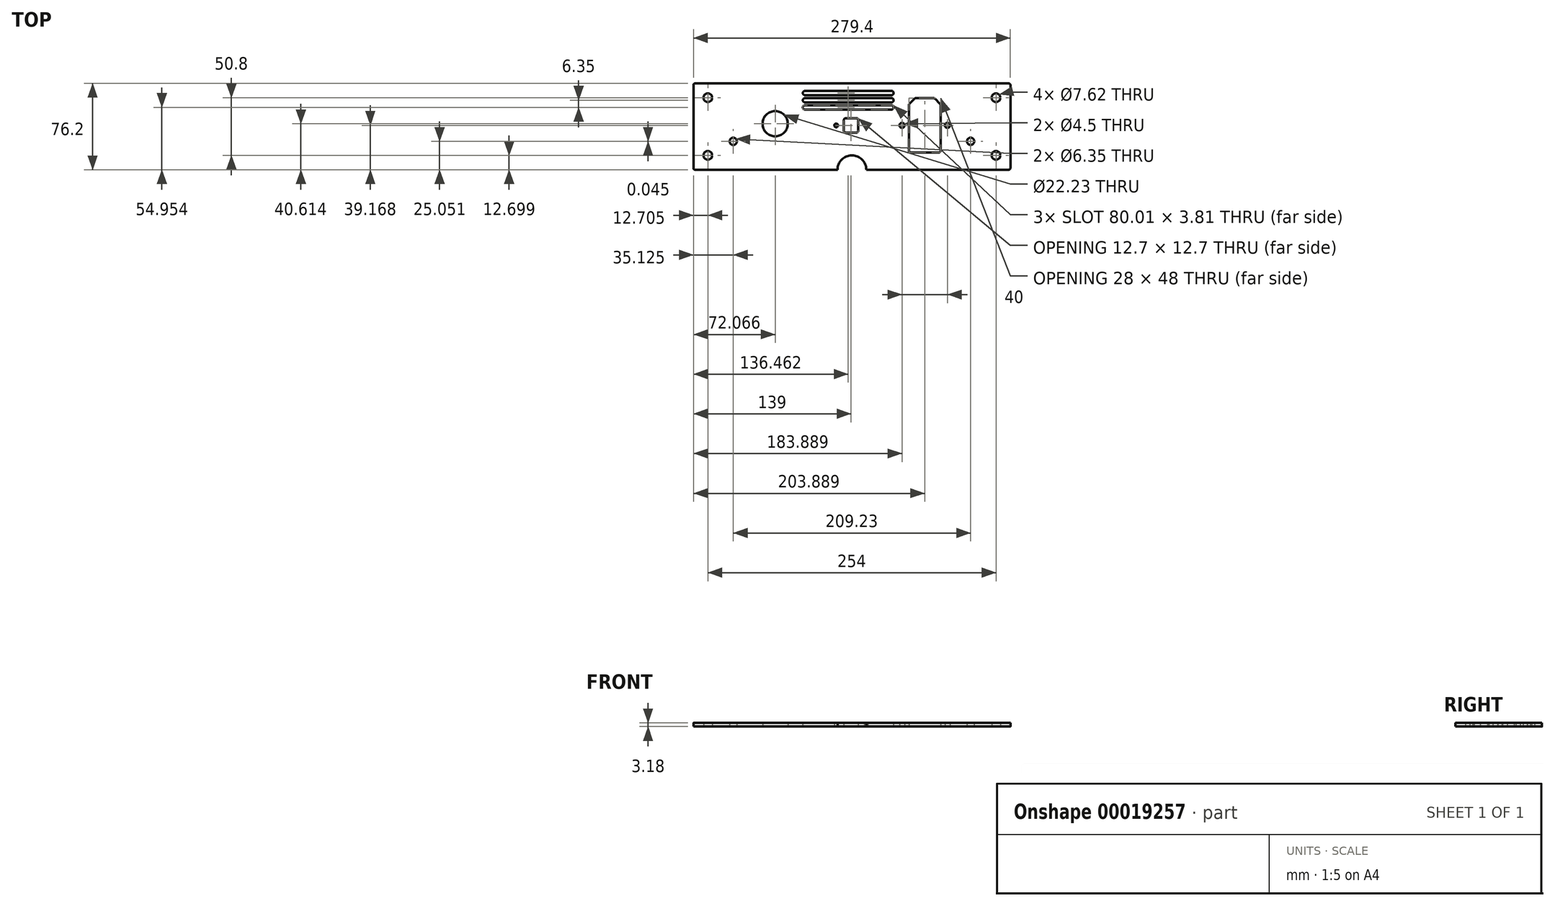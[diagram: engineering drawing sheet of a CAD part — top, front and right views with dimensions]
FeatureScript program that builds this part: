
annotation { "Feature Type Name" : "Feature", "Feature Type Description" : "" }
export const myFeature = defineFeature(function(context is Context, id is Id, definition is map)
    precondition{}
    {
        {
            var Q0;
            Q0=qCreatedBy(makeId("Top.planeOp"),FACE);
            var sketch = newSketch(context, id + "F0", { "sketchPlane" : qUnion([Q0])});
            skLineSegment(sketch, "E0.bottom", {"start": v(-124.13, 36.53) * mm, "end": v(152.02, 36.53) * mm});
            skLineSegment(sketch, "E0.left", {"start": v(-125.76, 34.9) * mm, "end": v(-125.76, -38.05) * mm});
            skLineSegment(sketch, "E0.right", {"start": v(153.64, 34.9) * mm, "end": v(153.64, -38.05) * mm});
            skLineSegment(sketch, "E1", {"start": v(-100.36, 36.53) * mm, "end": v(-100.36, -39.67) * mm, "construction": true});
            skLineSegment(sketch, "E2", {"start": v(128.24, 36.53) * mm, "end": v(128.24, -39.67) * mm, "construction": true});
            skCircle(sketch, "E3", {"center": v(-113.06, 23.83) * mm, "radius": 3.81 * mm});
            skCircle(sketch, "E4", {"center": v(-113.06, -26.97) * mm, "radius": 3.81 * mm});
            skCircle(sketch, "E5", {"center": v(140.94, 23.83) * mm, "radius": 3.81 * mm});
            skCircle(sketch, "E6", {"center": v(140.94, -26.97) * mm, "radius": 3.81 * mm});
            skLineSegment(sketch, "E7", {"start": v(-125.76, -24.75) * mm, "end": v(153.64, -24.75) * mm, "construction": true});
            skCircle(sketch, "E8", {"center": v(-53.7, 0.94) * mm, "radius": 11.11 * mm});
            skLineSegment(sketch, "E9.bottom", {"start": v(110.02, -4.48) * mm, "end": v(127.17, -4.48) * mm, "construction": true});
            skLineSegment(sketch, "E9.top", {"start": v(110.02, -24.67) * mm, "end": v(127.17, -24.67) * mm, "construction": true});
            skLineSegment(sketch, "E9.left", {"start": v(110.02, -4.48) * mm, "end": v(110.02, -24.67) * mm, "construction": true});
            skLineSegment(sketch, "E9.right", {"start": v(127.17, -4.48) * mm, "end": v(127.17, -24.67) * mm, "construction": true});
            skLineSegment(sketch, "E10.bottom", {"start": v(-99.2, -4.52) * mm, "end": v(-82.06, -4.52) * mm, "construction": true});
            skLineSegment(sketch, "E10.top", {"start": v(-99.2, -24.72) * mm, "end": v(-82.06, -24.72) * mm, "construction": true});
            skLineSegment(sketch, "E10.right", {"start": v(-82.06, -4.52) * mm, "end": v(-82.06, -24.72) * mm, "construction": true});
            skLineSegment(sketch, "E10.left", {"start": v(-99.2, -4.52) * mm, "end": v(-99.2, -24.72) * mm, "construction": true});
            skPoint(sketch, "E11.visualSharp", {"position": v(-125.76, 36.53) * mm});
            skArc(sketch, "E11.filletArc", {"start": v(-124.13, 36.53) * mm, "mid": v(-125.28, 36.05) * mm, "end": v(-125.76, 34.9) * mm});
            skPoint(sketch, "E12.visualSharp", {"position": v(-125.76, -39.67) * mm});
            skArc(sketch, "E12.filletArc", {"start": v(-125.76, -38.05) * mm, "mid": v(-125.28, -39.2) * mm, "end": v(-124.13, -39.67) * mm});
            skPoint(sketch, "E13.visualSharp", {"position": v(153.64, 36.53) * mm});
            skArc(sketch, "E13.filletArc", {"start": v(153.64, 34.9) * mm, "mid": v(153.17, 36.05) * mm, "end": v(152.02, 36.53) * mm});
            skPoint(sketch, "E14.visualSharp", {"position": v(153.64, -39.67) * mm});
            skArc(sketch, "E14.filletArc", {"start": v(152.02, -39.67) * mm, "mid": v(153.17, -39.2) * mm, "end": v(153.64, -38.05) * mm});
            skCircle(sketch, "E15", {"center": v(26.4, -0.6) * mm, "radius": 1.65 * mm});
            skCircle(sketch, "E16", {"center": v(0.08, -0.6) * mm, "radius": 1.65 * mm});
            skCircle(sketch, "E17", {"center": v(-53.7, 0.94) * mm, "radius": 19.98 * mm, "construction": true});
            skCircle(sketch, "E18", {"center": v(-90.64, -14.62) * mm, "radius": 3.18 * mm});
            skCircle(sketch, "E19", {"center": v(118.6, -14.57) * mm, "radius": 3.18 * mm});
            skLineSegment(sketch, "E20.bottom", {"start": v(70.46, 23.5) * mm, "end": v(85.8, 23.5) * mm});
            skLineSegment(sketch, "E20.top", {"start": v(65.75, -24.5) * mm, "end": v(90.5, -24.5) * mm});
            skLineSegment(sketch, "E20.left", {"start": v(64.13, 17.17) * mm, "end": v(64.13, -22.88) * mm});
            skLineSegment(sketch, "E20.right", {"start": v(92.13, 17.17) * mm, "end": v(92.13, -22.88) * mm});
            skLineSegment(sketch, "E21", {"start": v(78.13, -0.5) * mm, "end": v(98.13, -0.5) * mm, "construction": true});
            skLineSegment(sketch, "E22", {"start": v(78.13, -0.5) * mm, "end": v(58.13, -0.5) * mm, "construction": true});
            skCircle(sketch, "E23", {"center": v(58.13, -0.5) * mm, "radius": 2.25 * mm});
            skCircle(sketch, "E24", {"center": v(98.13, -0.5) * mm, "radius": 2.25 * mm});
            skLineSegment(sketch, "E25.bottom", {"start": v(8.52, 5.76) * mm, "end": v(17.96, 5.76) * mm});
            skLineSegment(sketch, "E25.top", {"start": v(8.52, -6.94) * mm, "end": v(17.96, -6.94) * mm});
            skLineSegment(sketch, "E25.left", {"start": v(6.9, 4.13) * mm, "end": v(6.9, -5.32) * mm});
            skLineSegment(sketch, "E25.right", {"start": v(19.6, 4.13) * mm, "end": v(19.6, -5.32) * mm});
            skLineSegment(sketch, "E26", {"start": v(-125.76, 11.13) * mm, "end": v(-100.36, 11.13) * mm, "construction": true});
            skLineSegment(sketch, "E27", {"start": v(-100.36, 11.13) * mm, "end": v(-125.76, 36.53) * mm, "construction": true});
            skLineSegment(sketch, "E28", {"start": v(-125.76, -14.27) * mm, "end": v(-100.36, -14.27) * mm, "construction": true});
            skLineSegment(sketch, "E29", {"start": v(-125.76, -14.27) * mm, "end": v(-100.36, -39.67) * mm, "construction": true});
            skLineSegment(sketch, "E30", {"start": v(-124.13, -39.67) * mm, "end": v(1.24, -39.67) * mm});
            skArc(sketch, "E31", {"start": v(26.64, -39.67) * mm, "mid": v(13.94, -26.97) * mm, "end": v(1.24, -39.67) * mm});
            skLineSegment(sketch, "E32.trimOffspring", {"start": v(26.64, -39.67) * mm, "end": v(152.02, -39.67) * mm});
            skLineSegment(sketch, "E33", {"start": v(64.6, 18.32) * mm, "end": v(69.31, 23.02) * mm});
            skLineSegment(sketch, "E34", {"start": v(86.95, 23.02) * mm, "end": v(91.65, 18.32) * mm});
            skLineSegment(sketch, "E35", {"start": v(0.08, -0.6) * mm, "end": v(26.4, -0.6) * mm, "construction": true});
            skLineSegment(sketch, "E36", {"start": v(13.24, 5.76) * mm, "end": v(13.24, -6.94) * mm, "construction": true});
            skLineSegment(sketch, "E37.0.right", {"start": v(-27.4, 26.08) * mm, "end": v(48.8, 26.08) * mm});
            skLineSegment(sketch, "E37.0.left", {"start": v(-27.4, 29.89) * mm, "end": v(48.8, 29.89) * mm});
            skLineSegment(sketch, "E38.direction1", {"start": v(-27.4, 15.28) * mm, "end": v(-27.4, 15.28) * mm});
            skLineSegment(sketch, "E38.0.2.0", {"start": v(-27.4, 27.98) * mm, "end": v(48.8, 27.98) * mm, "construction": true});
            skLineSegment(sketch, "E38.0.1.0", {"start": v(-27.4, 21.63) * mm, "end": v(48.8, 21.63) * mm, "construction": true});
            skLineSegment(sketch, "E37.1.left", {"start": v(-27.4, 23.54) * mm, "end": v(48.8, 23.54) * mm});
            skLineSegment(sketch, "E39.0.right", {"start": v(-27.4, 13.38) * mm, "end": v(48.8, 13.38) * mm});
            skLineSegment(sketch, "E39.0.left", {"start": v(-27.4, 17.19) * mm, "end": v(48.8, 17.19) * mm});
            skLineSegment(sketch, "E40", {"start": v(-27.4, 15.28) * mm, "end": v(48.8, 15.28) * mm, "construction": true});
            skLineSegment(sketch, "E37.1.right", {"start": v(-27.4, 19.73) * mm, "end": v(48.8, 19.73) * mm});
            skArc(sketch, "E39.0.endCap", {"start": v(48.8, 17.19) * mm, "mid": v(50.7, 15.28) * mm, "end": v(48.8, 13.38) * mm});
            skArc(sketch, "E37.1.endCap", {"start": v(48.8, 23.54) * mm, "mid": v(50.7, 21.63) * mm, "end": v(48.8, 19.73) * mm});
            skArc(sketch, "E37.0.endCap", {"start": v(48.8, 29.89) * mm, "mid": v(50.7, 27.98) * mm, "end": v(48.8, 26.08) * mm});
            skArc(sketch, "E37.1.startCap", {"start": v(-27.4, 19.73) * mm, "mid": v(-29.3, 21.63) * mm, "end": v(-27.4, 23.54) * mm});
            skArc(sketch, "E37.0.startCap", {"start": v(-27.4, 26.08) * mm, "mid": v(-29.3, 27.98) * mm, "end": v(-27.4, 29.89) * mm});
            skArc(sketch, "E39.0.startCap", {"start": v(-27.4, 13.38) * mm, "mid": v(-29.3, 15.28) * mm, "end": v(-27.4, 17.19) * mm});
            skPoint(sketch, "E41.visualSharp", {"position": v(6.9, 5.76) * mm});
            skArc(sketch, "E41.filletArc", {"start": v(8.52, 5.76) * mm, "mid": v(7.37, 5.28) * mm, "end": v(6.9, 4.13) * mm});
            skPoint(sketch, "E42.visualSharp", {"position": v(19.6, 5.76) * mm});
            skArc(sketch, "E42.filletArc", {"start": v(19.6, 4.13) * mm, "mid": v(19.11, 5.28) * mm, "end": v(17.96, 5.76) * mm});
            skPoint(sketch, "E43.visualSharp", {"position": v(19.6, -6.94) * mm});
            skArc(sketch, "E43.filletArc", {"start": v(17.96, -6.94) * mm, "mid": v(19.11, -6.47) * mm, "end": v(19.6, -5.32) * mm});
            skPoint(sketch, "E44.visualSharp", {"position": v(6.9, -6.94) * mm});
            skArc(sketch, "E44.filletArc", {"start": v(6.9, -5.32) * mm, "mid": v(7.37, -6.47) * mm, "end": v(8.52, -6.94) * mm});
            skPoint(sketch, "E45.visualSharp", {"position": v(64.13, 17.84) * mm});
            skArc(sketch, "E45.filletArc", {"start": v(64.6, 18.32) * mm, "mid": v(64.25, 17.8) * mm, "end": v(64.13, 17.17) * mm});
            skPoint(sketch, "E46.visualSharp", {"position": v(69.79, 23.5) * mm});
            skArc(sketch, "E46.filletArc", {"start": v(70.46, 23.5) * mm, "mid": v(69.84, 23.37) * mm, "end": v(69.31, 23.02) * mm});
            skPoint(sketch, "E47.visualSharp", {"position": v(86.47, 23.5) * mm});
            skArc(sketch, "E47.filletArc", {"start": v(86.95, 23.02) * mm, "mid": v(86.42, 23.37) * mm, "end": v(85.8, 23.5) * mm});
            skPoint(sketch, "E48.visualSharp", {"position": v(92.13, 17.84) * mm});
            skArc(sketch, "E48.filletArc", {"start": v(92.13, 17.17) * mm, "mid": v(92, 17.8) * mm, "end": v(91.65, 18.32) * mm});
            skPoint(sketch, "E49.visualSharp", {"position": v(92.13, -24.5) * mm});
            skArc(sketch, "E49.filletArc", {"start": v(90.5, -24.5) * mm, "mid": v(91.65, -24.03) * mm, "end": v(92.13, -22.88) * mm});
            skPoint(sketch, "E50.visualSharp", {"position": v(64.13, -24.5) * mm});
            skArc(sketch, "E50.filletArc", {"start": v(64.13, -22.88) * mm, "mid": v(64.6, -24.03) * mm, "end": v(65.75, -24.5) * mm});
            skSolve(sketch);
        }
        {
            var Q0;
            Q0=qSketchRegion(id+"F0",true);
            var Q1;
            {var subQ0=sQuery(id+"F0.wireOp",EDGE,"2bf4d64c-811b-49e9-8bac-2fb631b87969");Q1=makeQuery(id+"F0.imprint","IMPRINT",FACE,{"disambiguationData":[TD([[makeQuery(id+"F0.imprint","IMPRINT",EDGE,{"derivedFrom":subQ0}),-1.0]])]});}
            var Q2;
            Q2=makeQuery(id+"F0.imprint","IMPRINT",FACE,{"disambiguationData":[TD([[makeQuery(id+"F0.imprint","IMPRINT",EDGE,{"derivedFrom":sQuery(id+"F0.wireOp",EDGE,"E4")}),-1.0]])]});
            var Q3;
            Q3=makeQuery(id+"F0.imprint","IMPRINT",FACE,{"disambiguationData":[TD([[makeQuery(id+"F0.imprint","IMPRINT",EDGE,{"derivedFrom":sQuery(id+"F0.wireOp",EDGE,"2008dfa9-6c35-4ba0-b188-531ab9956baa.sketch_text.stroke-44")}),-1.0]])]});
            var Q4;
            Q4=makeQuery(id+"F0.imprint","IMPRINT",FACE,{"disambiguationData":[TD([[makeQuery(id+"F0.imprint","IMPRINT",EDGE,{"derivedFrom":sQuery(id+"F0.wireOp",EDGE,"eab93db6-d5a0-4661-8d19-a60daf389fbf.sketch_text.stroke-16")}),1.0]])]});
            var Q5;
            Q5=makeQuery(id+"F0.imprint","IMPRINT",FACE,{"disambiguationData":[TD([[makeQuery(id+"F0.imprint","IMPRINT",EDGE,{"derivedFrom":sQuery(id+"F0.wireOp",EDGE,"E9.bottom")}),1.0]])]});
            var Q6;
            Q6=makeQuery(id+"F0.imprint","IMPRINT",FACE,{"disambiguationData":[TD([[makeQuery(id+"F0.imprint","IMPRINT",EDGE,{"derivedFrom":sQuery(id+"F0.wireOp",EDGE,"6bf0a539-61ef-4557-94e5-60696c5db384.bottom")}),1.0]])]});
            var Q7;
            Q7=makeQuery(id+"F0.imprint","IMPRINT",FACE,{"disambiguationData":[TD([[makeQuery(id+"F0.imprint","IMPRINT",EDGE,{"derivedFrom":sQuery(id+"F0.wireOp",EDGE,"2008dfa9-6c35-4ba0-b188-531ab9956baa.sketch_text.stroke-62")}),1.0]])]});
            var Q8;
            Q8=makeQuery(id+"F0.imprint","IMPRINT",FACE,{"disambiguationData":[TD([[makeQuery(id+"F0.imprint","IMPRINT",EDGE,{"derivedFrom":sQuery(id+"F0.wireOp",EDGE,"E10.bottom")}),-1.0]])]});
            var Q9;
            Q9=makeQuery(id+"F0.imprint","IMPRINT",FACE,{"disambiguationData":[TD([[makeQuery(id+"F0.imprint","IMPRINT",EDGE,{"derivedFrom":sQuery(id+"F0.wireOp",EDGE,"E8")}),-1.0]])]});
            var Q10;
            Q10=makeQuery(id+"F0.imprint","IMPRINT",FACE,{"disambiguationData":[TD([[makeQuery(id+"F0.imprint","IMPRINT",EDGE,{"derivedFrom":sQuery(id+"F0.wireOp",EDGE,"E3")}),-1.0]])]});
            var Q11;
            Q11=makeQuery(id+"F0.imprint","IMPRINT",FACE,{"disambiguationData":[TD([[makeQuery(id+"F0.imprint","IMPRINT",EDGE,{"derivedFrom":sQuery(id+"F0.wireOp",EDGE,"eab93db6-d5a0-4661-8d19-a60daf389fbf.sketch_text.stroke-0")}),1.0]])]});
            var Q12;
            Q12=makeQuery(id+"F0.imprint","IMPRINT",FACE,{"disambiguationData":[TD([[makeQuery(id+"F0.imprint","IMPRINT",EDGE,{"derivedFrom":sQuery(id+"F0.wireOp",EDGE,"d8af0bd6-aaca-4bc3-8748-92abea86f275.sketch_text.stroke-43")}),-1.0]])]});
            var Q13;
            Q13=makeQuery(id+"F0.imprint","IMPRINT",FACE,{"disambiguationData":[TD([[makeQuery(id+"F0.imprint","IMPRINT",EDGE,{"derivedFrom":sQuery(id+"F0.wireOp",EDGE,"2008dfa9-6c35-4ba0-b188-531ab9956baa.sketch_text.stroke-95")}),1.0]])]});
            var Q14;
            Q14=makeQuery(id+"F0.imprint","IMPRINT",FACE,{"disambiguationData":[TD([[makeQuery(id+"F0.imprint","IMPRINT",EDGE,{"derivedFrom":sQuery(id+"F0.wireOp",EDGE,"d8af0bd6-aaca-4bc3-8748-92abea86f275.sketch_text.stroke-0")}),-1.0]])]});
            var Q15;
            Q15=makeQuery(id+"F0.imprint","IMPRINT",FACE,{"disambiguationData":[TD([[makeQuery(id+"F0.imprint","IMPRINT",EDGE,{"derivedFrom":sQuery(id+"F0.wireOp",EDGE,"eab93db6-d5a0-4661-8d19-a60daf389fbf.sketch_text.stroke-80")}),-1.0]])]});
            var Q16;
            Q16=makeQuery(id+"F0.imprint","IMPRINT",FACE,{"disambiguationData":[TD([[makeQuery(id+"F0.imprint","IMPRINT",EDGE,{"derivedFrom":sQuery(id+"F0.wireOp",EDGE,"eab93db6-d5a0-4661-8d19-a60daf389fbf.sketch_text.stroke-60")}),-1.0]])]});
            var Q17;
            Q17=makeQuery(id+"F0.imprint","IMPRINT",FACE,{"disambiguationData":[TD([[makeQuery(id+"F0.imprint","IMPRINT",EDGE,{"derivedFrom":sQuery(id+"F0.wireOp",EDGE,"2008dfa9-6c35-4ba0-b188-531ab9956baa.sketch_text.stroke-80")}),-1.0]])]});
            var Q18;
            Q18=makeQuery(id+"F0.imprint","IMPRINT",FACE,{"disambiguationData":[TD([[makeQuery(id+"F0.imprint","IMPRINT",EDGE,{"derivedFrom":sQuery(id+"F0.wireOp",EDGE,"d8af0bd6-aaca-4bc3-8748-92abea86f275.sketch_text.stroke-62")}),1.0]])]});
            var Q19;
            Q19=makeQuery(id+"F0.imprint","IMPRINT",FACE,{"disambiguationData":[TD([[makeQuery(id+"F0.imprint","IMPRINT",EDGE,{"derivedFrom":sQuery(id+"F0.wireOp",EDGE,"E6")}),-1.0]])]});
            var Q20;
            Q20=makeQuery(id+"F0.imprint","IMPRINT",FACE,{"disambiguationData":[TD([[makeQuery(id+"F0.imprint","IMPRINT",EDGE,{"derivedFrom":sQuery(id+"F0.wireOp",EDGE,"eab93db6-d5a0-4661-8d19-a60daf389fbf.sketch_text.stroke-16")}),-1.0]])]});
            var Q21;
            Q21=makeQuery(id+"F0.imprint","IMPRINT",FACE,{"disambiguationData":[TD([[makeQuery(id+"F0.imprint","IMPRINT",EDGE,{"derivedFrom":sQuery(id+"F0.wireOp",EDGE,"E5")}),-1.0]])]});
            var Q22;
            Q22=makeQuery(id+"F0.imprint","IMPRINT",FACE,{"disambiguationData":[TD([[makeQuery(id+"F0.imprint","IMPRINT",EDGE,{"derivedFrom":sQuery(id+"F0.wireOp",EDGE,"2008dfa9-6c35-4ba0-b188-531ab9956baa.sketch_text.stroke-62")}),-1.0]])]});
            var Q23;
            Q23=makeQuery(id+"F0.imprint","IMPRINT",FACE,{"disambiguationData":[TD([[makeQuery(id+"F0.imprint","IMPRINT",EDGE,{"derivedFrom":sQuery(id+"F0.wireOp",EDGE,"2008dfa9-6c35-4ba0-b188-531ab9956baa.sketch_text.stroke-0")}),-1.0]])]});
            var Q24;
            Q24=makeQuery(id+"F0.imprint","IMPRINT",FACE,{"disambiguationData":[TD([[makeQuery(id+"F0.imprint","IMPRINT",EDGE,{"derivedFrom":sQuery(id+"F0.wireOp",EDGE,"af9f44e2-9865-4e7a-8dc2-1ac1fc63666f")}),1.0]])]});
            var Q25;
            Q25=makeQuery(id+"F0.imprint","IMPRINT",FACE,{"disambiguationData":[TD([[makeQuery(id+"F0.imprint","IMPRINT",EDGE,{"derivedFrom":sQuery(id+"F0.wireOp",EDGE,"E9.bottom")}),-1.0]])]});
            var Q26;
            Q26=makeQuery(id+"F0.imprint","IMPRINT",FACE,{"disambiguationData":[TD([[makeQuery(id+"F0.imprint","IMPRINT",EDGE,{"derivedFrom":sQuery(id+"F0.wireOp",EDGE,"eab93db6-d5a0-4661-8d19-a60daf389fbf.sketch_text.stroke-0")}),-1.0]])]});
            var Q27;
            {var subQ6=sQuery(id+"F0.wireOp",EDGE,"eab93db6-d5a0-4661-8d19-a60daf389fbf.sketch_text.stroke-35");Q27=makeQuery(id+"F0.imprint","IMPRINT",FACE,{"disambiguationData":[TD([[makeQuery(id+"F0.imprint","IMPRINT",EDGE,{"derivedFrom":subQ6}),-1.0]])]});}
            var Q28;
            Q28=makeQuery(id+"F0.imprint","IMPRINT",FACE,{"disambiguationData":[TD([[makeQuery(id+"F0.imprint","IMPRINT",EDGE,{"derivedFrom":sQuery(id+"F0.wireOp",EDGE,"d8af0bd6-aaca-4bc3-8748-92abea86f275.sketch_text.stroke-15")}),-1.0]])]});
            var Q29;
            Q29=makeQuery(id+"F0.imprint","IMPRINT",FACE,{"disambiguationData":[TD([[makeQuery(id+"F0.imprint","IMPRINT",EDGE,{"derivedFrom":sQuery(id+"F0.wireOp",EDGE,"2008dfa9-6c35-4ba0-b188-531ab9956baa.sketch_text.stroke-16")}),-1.0]])]});
            var Q30;
            {var subQ3=sQuery(id+"F0.wireOp",EDGE,"eab93db6-d5a0-4661-8d19-a60daf389fbf.sketch_text.stroke-11");Q30=makeQuery(id+"F0.imprint","IMPRINT",FACE,{"disambiguationData":[TD([[makeQuery(id+"F0.imprint","IMPRINT",EDGE,{"derivedFrom":subQ3}),-1.0]])]});}
            var Q31;
            {var subQ4=sQuery(id+"F0.wireOp",EDGE,"eab93db6-d5a0-4661-8d19-a60daf389fbf.sketch_text.stroke-35");Q31=makeQuery(id+"F0.imprint","IMPRINT",FACE,{"disambiguationData":[TD([[makeQuery(id+"F0.imprint","IMPRINT",EDGE,{"derivedFrom":subQ4}),1.0]])]});}
            var Q32;
            {var subQ4=sQuery(id+"F0.wireOp",EDGE,"eab93db6-d5a0-4661-8d19-a60daf389fbf.sketch_text.stroke-25");Q32=makeQuery(id+"F0.imprint","IMPRINT",FACE,{"disambiguationData":[TD([[makeQuery(id+"F0.imprint","IMPRINT",EDGE,{"derivedFrom":subQ4}),-1.0]])]});}
            var Q33;
            {var subQ6=sQuery(id+"F0.wireOp",EDGE,"eab93db6-d5a0-4661-8d19-a60daf389fbf.sketch_text.stroke-65");Q33=makeQuery(id+"F0.imprint","IMPRINT",FACE,{"disambiguationData":[TD([[makeQuery(id+"F0.imprint","IMPRINT",EDGE,{"derivedFrom":subQ6}),-1.0]])]});}
            var Q34;
            {var subQ0=sQuery(id+"F0.wireOp",EDGE,"eab93db6-d5a0-4661-8d19-a60daf389fbf.sketch_text.stroke-59");Q34=makeQuery(id+"F0.imprint","IMPRINT",FACE,{"disambiguationData":[TD([[makeQuery(id+"F0.imprint","IMPRINT",EDGE,{"derivedFrom":subQ0}),-1.0]])]});}
            var Q35;
            {var subQ3=sQuery(id+"F0.wireOp",EDGE,"eab93db6-d5a0-4661-8d19-a60daf389fbf.sketch_text.stroke-38");Q35=makeQuery(id+"F0.imprint","IMPRINT",FACE,{"disambiguationData":[TD([[makeQuery(id+"F0.imprint","IMPRINT",EDGE,{"derivedFrom":subQ3}),-1.0]])]});}
            var Q36;
            Q36=makeQuery(id+"F0.imprint","IMPRINT",FACE,{"disambiguationData":[TD([[makeQuery(id+"F0.imprint","IMPRINT",EDGE,{"derivedFrom":sQuery(id+"F0.wireOp",EDGE,"d8af0bd6-aaca-4bc3-8748-92abea86f275.sketch_text.stroke-55")}),1.0]])]});
            var Q37;
            Q37=makeQuery(id+"F0.imprint","IMPRINT",FACE,{"disambiguationData":[TD([[makeQuery(id+"F0.imprint","IMPRINT",EDGE,{"derivedFrom":sQuery(id+"F0.wireOp",EDGE,"eab93db6-d5a0-4661-8d19-a60daf389fbf.sketch_text.stroke-60")}),1.0]])]});
            var Q38;
            {var subQ3=sQuery(id+"F0.wireOp",EDGE,"eab93db6-d5a0-4661-8d19-a60daf389fbf.sketch_text.stroke-86");Q38=makeQuery(id+"F0.imprint","IMPRINT",FACE,{"disambiguationData":[TD([[makeQuery(id+"F0.imprint","IMPRINT",EDGE,{"derivedFrom":subQ3}),-1.0]])]});}
            var Q39;
            Q39=makeQuery(id+"F0.imprint","IMPRINT",FACE,{"disambiguationData":[TD([[makeQuery(id+"F0.imprint","IMPRINT",EDGE,{"derivedFrom":sQuery(id+"F0.wireOp",EDGE,"2008dfa9-6c35-4ba0-b188-531ab9956baa.sketch_text.stroke-12")}),-1.0]])]});
            var Q40;
            Q40=makeQuery(id+"F0.imprint","IMPRINT",FACE,{"disambiguationData":[TD([[makeQuery(id+"F0.imprint","IMPRINT",EDGE,{"derivedFrom":sQuery(id+"F0.wireOp",EDGE,"716e3c6b-710e-4345-be30-ddb08bf85246.bottom")}),-1.0]])]});
            var Q41;
            {var subQ3=sQuery(id+"F0.wireOp",EDGE,"E28");Q41=makeQuery(id+"F0.imprint","IMPRINT",FACE,{"disambiguationData":[TD([[makeQuery(id+"F0.imprint","IMPRINT",EDGE,{"derivedFrom":subQ3}),-1.0]])]});}
            extrude(context, id + "F1", {"entities" : qUnion([Q0, Q1, Q2, Q3, Q4, Q5, Q6, Q7, Q8, Q9, Q10, Q11, Q12, Q13, Q14, Q15, Q16, Q17, Q18, Q19, Q20, Q21, Q22, Q23, Q24, Q25, Q26, Q27, Q28, Q29, Q30, Q31, Q32, Q33, Q34, Q35, Q36, Q37, Q38, Q39, Q40, Q41]), "depth" : 3.17 * mm});
        }
    });
